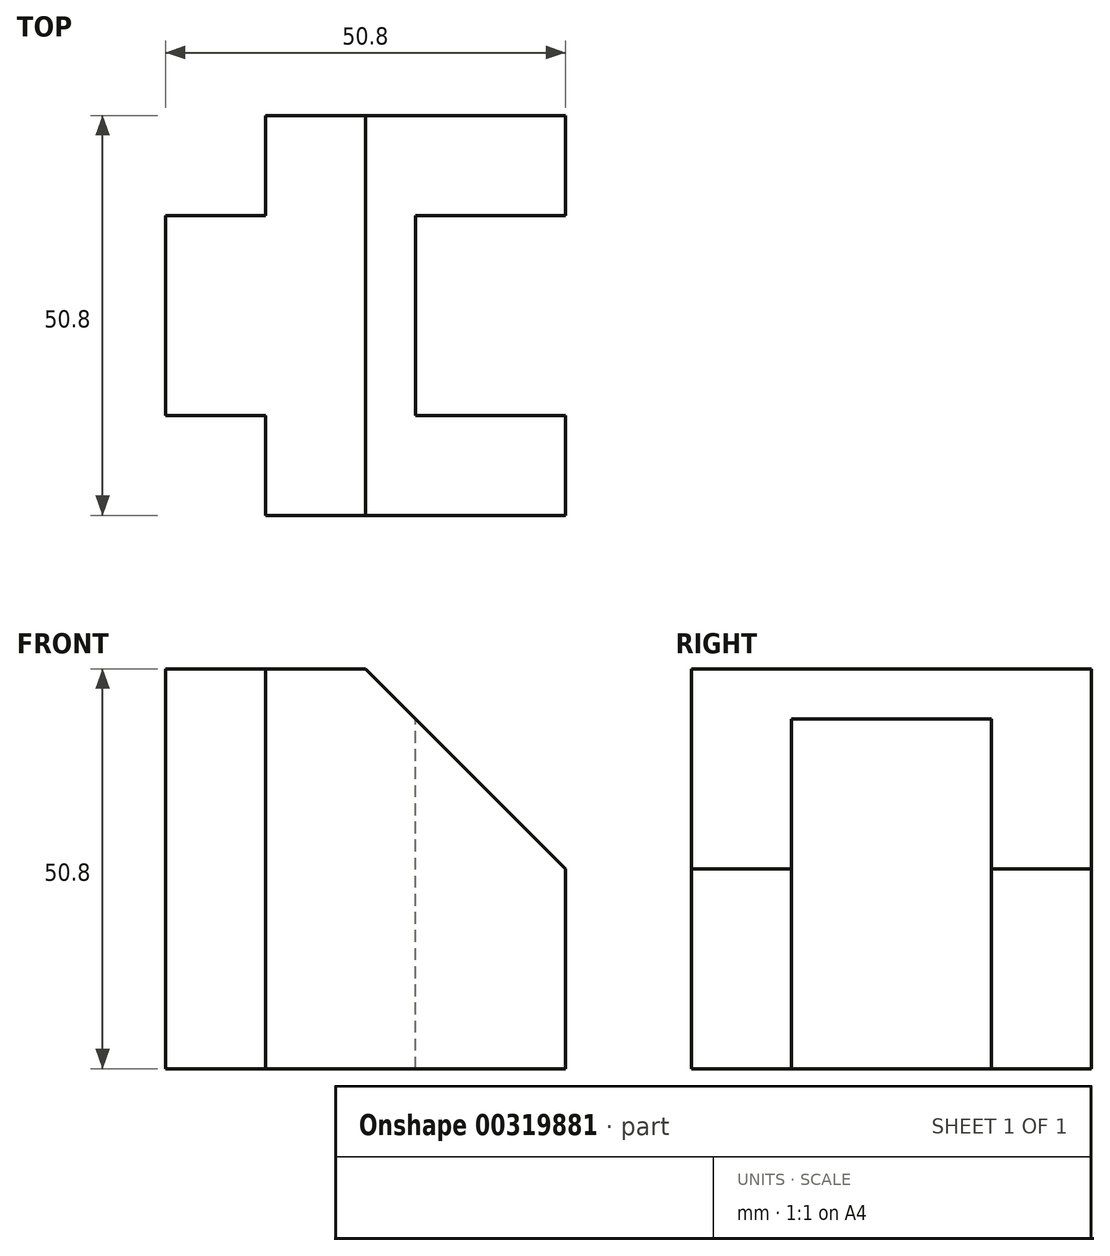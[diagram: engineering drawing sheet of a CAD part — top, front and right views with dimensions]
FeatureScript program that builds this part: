
annotation { "Feature Type Name" : "Feature", "Feature Type Description" : "" }
export const myFeature = defineFeature(function(context is Context, id is Id, definition is map)
    precondition{}
    {
        {
            var Q0;
            Q0=qCreatedBy(makeId("Front.planeOp"),FACE);
            var sketch = newSketch(context, id + "F0", { "sketchPlane" : qUnion([Q0])});
            skLineSegment(sketch, "E0.bottom", {"start": v(0, 0) * mm, "end": v(12.7, 0) * mm});
            skLineSegment(sketch, "E0.top", {"start": v(0, 50.8) * mm, "end": v(12.7, 50.8) * mm});
            skLineSegment(sketch, "E0.left", {"start": v(0, 0) * mm, "end": v(0, 50.8) * mm});
            skLineSegment(sketch, "E0.right", {"start": v(12.7, 0) * mm, "end": v(12.7, 50.8) * mm});
            skLineSegment(sketch, "E1", {"start": v(12.7, 0) * mm, "end": v(50.8, 0) * mm});
            skLineSegment(sketch, "E2", {"start": v(12.7, 50.8) * mm, "end": v(25.4, 50.8) * mm});
            skLineSegment(sketch, "E3", {"start": v(50.8, 0) * mm, "end": v(50.8, 25.4) * mm});
            skLineSegment(sketch, "E4", {"start": v(50.8, 25.4) * mm, "end": v(25.4, 50.8) * mm});
            skSolve(sketch);
        }
        {
            var Q0;
            Q0=makeQuery(id+"F0.imprint","IMPRINT",FACE,{"disambiguationData":[TD([[makeQuery(id+"F0.imprint","IMPRINT",EDGE,{"derivedFrom":sQuery(id+"F0.wireOp",EDGE,"E0.bottom")}),1.0]])]});
            extrude(context, id + "F1", {"entities" : qUnion([Q0]), "endBound" : BoundingType.SYMMETRIC, "depth" : 25.4 * mm});
        }
        {
            var Q0;
            Q0=makeQuery(id+"F0.imprint","IMPRINT",FACE,{"disambiguationData":[TD([[makeQuery(id+"F0.imprint","IMPRINT",EDGE,{"derivedFrom":sQuery(id+"F0.wireOp",EDGE,"E0.right")}),-1.0]])]});
            extrude(context, id + "F2", {"entities" : qUnion([Q0]), "operationType" : NewBodyOperationType.ADD, "endBound" : BoundingType.SYMMETRIC, "depth" : 50.8 * mm});
        }
        {
            var Q0;
            Q0=makeQuery(id+"F2.opExtrude","SWEPT_FACE",FACE,{"disambiguationData":[OSD([sQuery(id+"F0.wireOp",EDGE,"E3")])]});
            var sketch = newSketch(context, id + "F3", { "sketchPlane" : qUnion([Q0])});
            skLineSegment(sketch, "E5", {"start": v(-12.7, 0) * mm, "end": v(-12.7, 44.45) * mm});
            skLineSegment(sketch, "E6", {"start": v(-12.7, 44.45) * mm, "end": v(12.7, 44.45) * mm});
            skLineSegment(sketch, "E7", {"start": v(12.7, 44.45) * mm, "end": v(12.7, 0) * mm});
            skSolve(sketch);
        }
        {
            var Q0;
            Q0 = qSketchRegion(id + "F3", true);
            var Q1;
            {var subQ0=sQuery(id+"F3.wireOp",EDGE,"E5");var subQ1=sQuery(id+"F0.wireOp",EDGE,"E3");var subQ2=makeQuery(id+"F2.opExtrude","SWEPT_EDGE",EDGE,{"disambiguationData":[OSD([sQuery(id+"F0.wireOp",EDGE,"E1"),subQ1])]});var subQ3=makeQuery(id+"F3.imprint","INTERSECT",VERTEX,{"derivedFrom":[subQ2,subQ0]});Q1=makeQuery(id+"F3.imprint","IMPRINT",FACE,{"disambiguationData":[TD([[makeQuery(id+"F3.imprint","IMPRINT",EDGE,{"disambiguationData":[TD([[subQ3,-1.0]])],"derivedFrom":subQ0}),-1.0]])]});}
            var Q2;
            {var subQ0=sQuery(id+"F3.wireOp",EDGE,"E6");Q2=makeQuery(id+"F3.imprint","IMPRINT",FACE,{"disambiguationData":[TD([[makeQuery(id+"F3.imprint","IMPRINT",EDGE,{"derivedFrom":subQ0}),-1.0]])]});}
            extrude(context, id + "F4", {"entities" : qUnion([Q0, Q1, Q2]), "operationType" : NewBodyOperationType.REMOVE, "oppositeDirection" : true, "depth" : 19.05 * mm});
        }
    });
